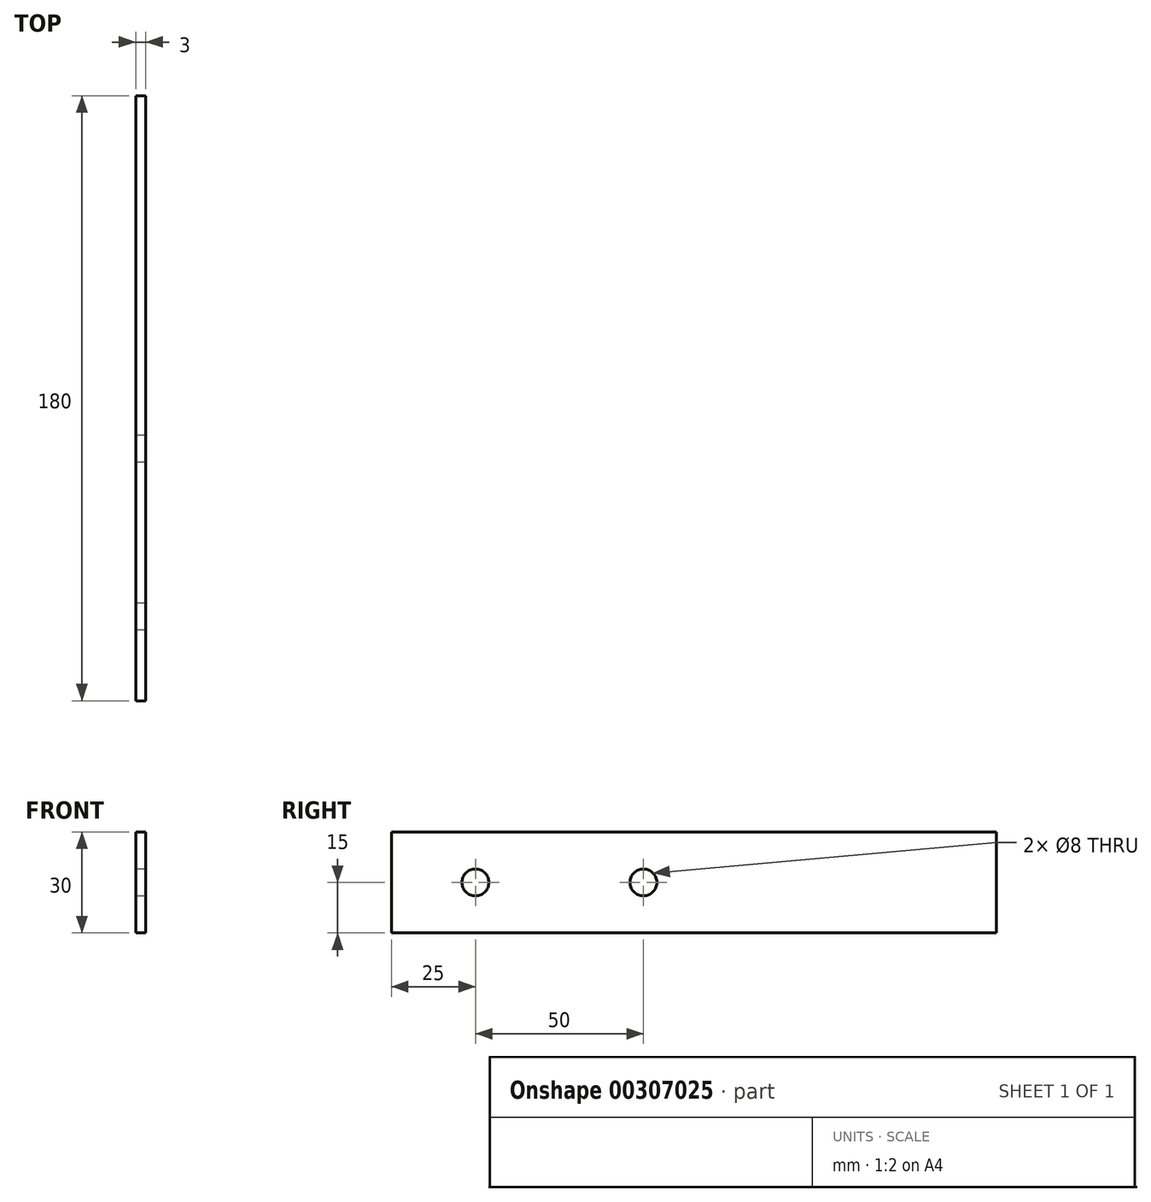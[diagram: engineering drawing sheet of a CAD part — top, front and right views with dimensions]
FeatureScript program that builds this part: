
annotation { "Feature Type Name" : "Feature", "Feature Type Description" : "" }
export const myFeature = defineFeature(function(context is Context, id is Id, definition is map)
    precondition{}
    {
        {
            var Q0;
            Q0=qCreatedBy(makeId("Front.planeOp"),FACE);
            var sketch = newSketch(context, id + "F0", { "sketchPlane" : qUnion([Q0])});
            skLineSegment(sketch, "E0", {"start": v(0, 40) * mm, "end": v(0, 10) * mm});
            skLineSegment(sketch, "E1", {"start": v(0, 10) * mm, "end": v(3, 10) * mm});
            skLineSegment(sketch, "E2", {"start": v(3, 10) * mm, "end": v(3, 40) * mm});
            skLineSegment(sketch, "E3", {"start": v(3, 40) * mm, "end": v(0, 40) * mm});
            skSolve(sketch);
        }
        {
            var Q0;
            Q0=qSketchRegion(id+"F0",true);
            extrude(context, id + "F1", {"entities" : qUnion([Q0]), "depth" : 180 * mm});
        }
        {
            var Q0;
            Q0=makeQuery(id+"F1.opExtrude","SWEPT_FACE",FACE,{"disambiguationData":[OSD([sQuery(id+"F0.wireOp",EDGE,"E0")])]});
            var sketch = newSketch(context, id + "F2", { "sketchPlane" : qUnion([Q0])});
            skCircle(sketch, "E4", {"center": v(155, 25) * mm, "radius": 4 * mm});
            skCircle(sketch, "E5", {"center": v(105, 25) * mm, "radius": 4 * mm});
            skSolve(sketch);
        }
        {
            var Q0;
            Q0 = qSketchRegion(id + "F2", true);
            extrude(context, id + "F3", {"entities" : qUnion([Q0]), "operationType" : NewBodyOperationType.REMOVE, "oppositeDirection" : true, "depth" : 25 * mm});
        }
    });
